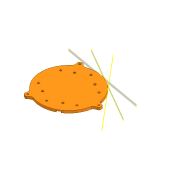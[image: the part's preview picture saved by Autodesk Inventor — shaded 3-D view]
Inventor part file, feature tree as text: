
AUTODESK INVENTOR PART (.ipt)
format: ipt  version: 2020.3 (Build 243373000, 373)  size: 300,544 bytes
history: native  units: mm
features: extrude x8, sketch x4, plane x3, fillet x2, pattern_circular x1
ambient origin geometry x8: Origin, YZ Plane, XZ Plane, XY Plane, X Axis, Y Axis, Z Axis, Center Point
bodies: Solid1 (feature_tree)
feature tree (18):
  sketch  "Sketch1"  dims[d0=95.0mm d1=120.0deg]
  extrude  "Extrusion1"  TaperAngle=120.0deg  [1 undecoded]
  plane  "Work Plane1"
  plane  "Work Plane2"
  plane  "Work Plane3"
  extrude  "Extrusion2"  Depth=16.0mm
  extrude  "Extrusion3"  Depth=6.0mm
  sketch  "Sketch2"  dims[d2=120.0deg d3=16.0mm]
  sketch  "Sketch3"  dims[d4=3.0mm d5=6.0mm]
  extrude  "Extrusion4"  Depth=10.0mm
  extrude  "Extrusion5"  Depth=10.0mm
  extrude  "Extrusion6"  Depth=10.0mm
  fillet  "Fillet1"  Radius=1.2mm
  fillet  "Fillet2"  Radius=4.0mm
  extrude  "Extrusion7"  Depth=10.0mm TaperAngle=360.0deg
  pattern_circular  "Circular Pattern1"  [2 undecoded]
  extrude  "Extrusion8"  Depth=10.0mm
  sketch  "Sketch4"  dims[d6=1.0mm d7=10.0mm d8=3.6mm d9=2.4mm d10=1.2mm d11=4.0mm d12=0.0mm d13=30.0mm d15=360.0deg d17=9.6mm d18=12.0mm d19=2.0mm d20=6.0mm d21=2.0mm d23=60.0deg d24=6.1mm d25=8.0mm d26=6.1mm d27=60.0deg d28=3.490659mm d29=3.490659mm d39=90.0deg d40=90.0deg d41=90.0deg d42=5.0mm d43=0.0mm d44=2.0mm d45=0.0mm d46=5.5mm d47=5.5mm d48=5.5mm d49=24.0mm d50=0.0mm d51=24.0mm d52=0.0mm d53=24.0mm d54=0.0mm d55=6.0mm d56=40.0mm d57=60.0mm d58=3.2mm d59=1.0mm d60=1.0mm d61=1.0mm d62=1.0mm d63=6.0mm d64=3.0mm d65=8.0mm d66=6.0mm d67=10.0mm d68=0.0mm d69=60.0mm d70=360.0deg d72=10.0mm d73=0.0mm d74=0.5mm d75=0.872665mm d76=0.5mm d77=0.872665mm]
note: 3 required parameter values undecoded (feature->parameter linkage not recoverable at this tier; creation-order binding heuristic only, values carry confidence <= 0.55)
